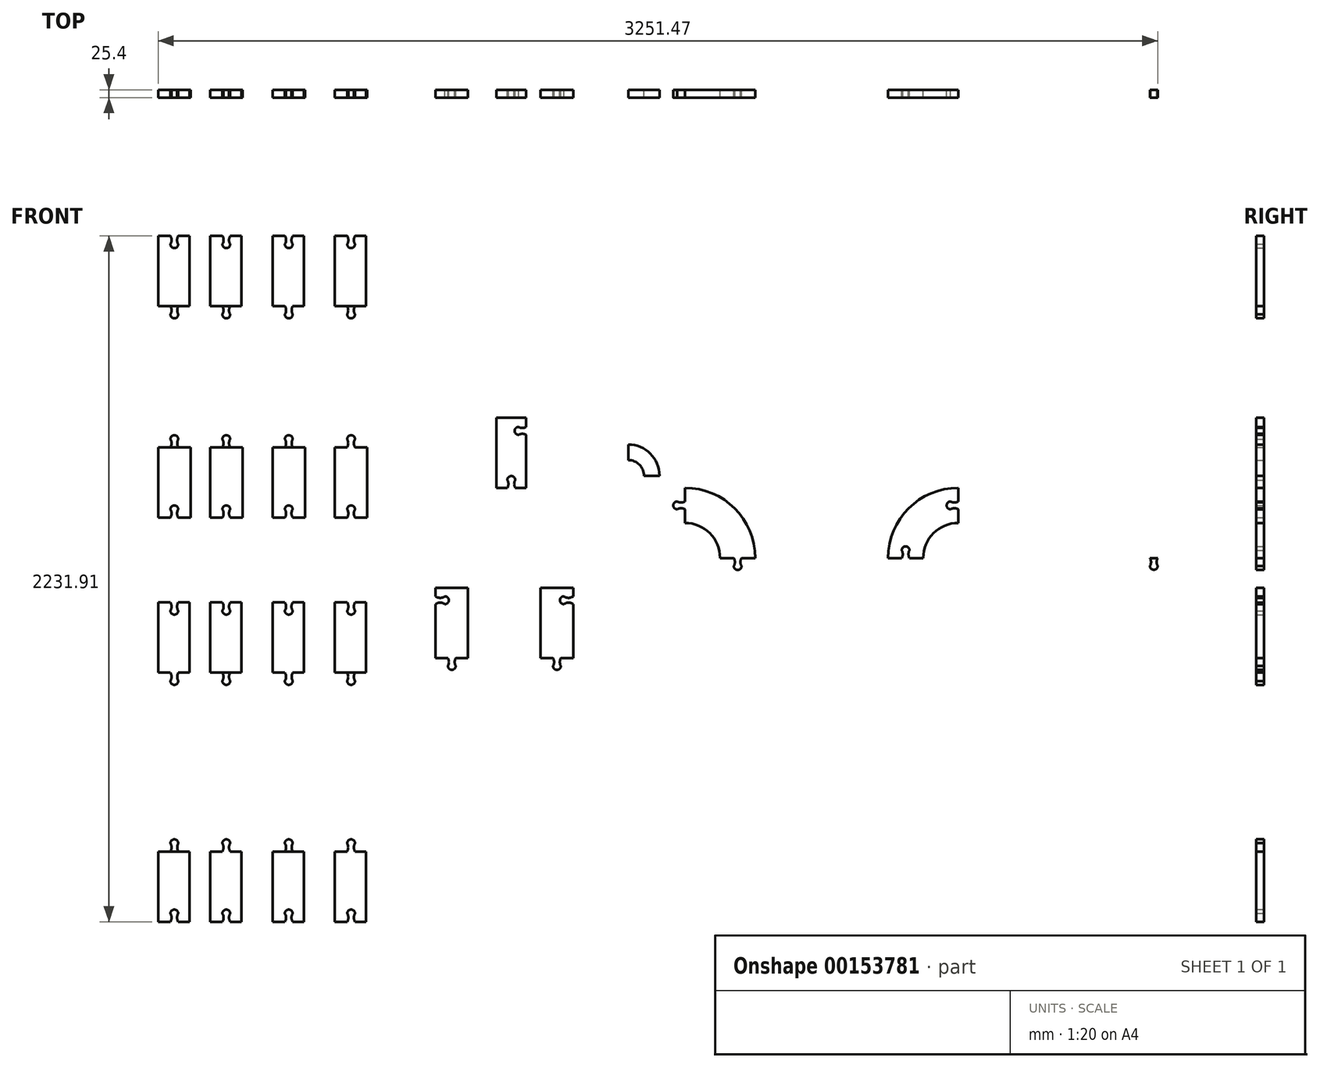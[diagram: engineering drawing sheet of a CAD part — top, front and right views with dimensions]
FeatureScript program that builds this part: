
annotation { "Feature Type Name" : "Feature", "Feature Type Description" : "" }
export const myFeature = defineFeature(function(context is Context, id is Id, definition is map)
    precondition{}
    {
        {
            var Q0;
            Q0=qCreatedBy(makeId("Front.planeOp"),FACE);
            var sketch = newSketch(context, id + "F0", { "sketchPlane" : qUnion([Q0])});
            skLineSegment(sketch, "E0", {"start": v(-147.56, 131.5) * mm, "end": v(-147.56, -97.1) * mm});
            skLineSegment(sketch, "E1", {"start": v(-147.56, 131.5) * mm, "end": v(-41.94, 131.5) * mm});
            skLineSegment(sketch, "E2", {"start": v(-41.94, 131.5) * mm, "end": v(-41.94, -97.1) * mm});
            skArc(sketch, "E3", {"start": v(-82.05, 158.39) * mm, "mid": v(-94.75, 171.09) * mm, "end": v(-107.45, 158.39) * mm});
            skArc(sketch, "E4", {"start": v(-107.45, 131.5) * mm, "mid": v(-103.6, 144.95) * mm, "end": v(-107.45, 158.39) * mm});
            skArc(sketch, "E5", {"start": v(-82.05, 158.39) * mm, "mid": v(-85.44, 144.95) * mm, "end": v(-82.05, 131.5) * mm});
            skPoint(sketch, "E6.start.orphan", {"position": v(-94.75, 131.5) * mm});
            skArc(sketch, "E7", {"start": v(-82.05, -70.22) * mm, "mid": v(-94.75, -57.52) * mm, "end": v(-107.45, -70.22) * mm});
            skArc(sketch, "E8", {"start": v(-107.45, -97.1) * mm, "mid": v(-103.6, -83.66) * mm, "end": v(-107.45, -70.22) * mm});
            skArc(sketch, "E9", {"start": v(-82.05, -70.22) * mm, "mid": v(-85.9, -83.66) * mm, "end": v(-82.05, -97.1) * mm});
            skPoint(sketch, "E10.start.orphan", {"position": v(-94.75, -97.1) * mm});
            skLineSegment(sketch, "E11", {"start": v(-147.56, -97.1) * mm, "end": v(-107.45, -97.1) * mm});
            skLineSegment(sketch, "E12", {"start": v(-82.05, -97.1) * mm, "end": v(-41.94, -97.1) * mm});
            skLineSegment(sketch, "E13", {"start": v(-10.22, 162) * mm, "end": v(-10.22, -91.05) * mm});
            skLineSegment(sketch, "E14.MirrorCS", {"start": v(61.6, -97.1) * mm, "end": v(21.5, -97.1) * mm});
            skArc(sketch, "E15.MirrorCS", {"start": v(61.6, 158.39) * mm, "mid": v(74.3, 171.09) * mm, "end": v(87, 158.39) * mm});
            skLineSegment(sketch, "E16.MirrorCS", {"start": v(127.12, -97.1) * mm, "end": v(87, -97.1) * mm});
            skArc(sketch, "E17.MirrorCS", {"start": v(61.6, -70.22) * mm, "mid": v(74.3, -57.52) * mm, "end": v(87, -70.22) * mm});
            skArc(sketch, "E18.MirrorCS", {"start": v(61.6, -70.22) * mm, "mid": v(65.45, -83.66) * mm, "end": v(61.6, -97.1) * mm});
            skArc(sketch, "E19.MirrorCS", {"start": v(87, -97.1) * mm, "mid": v(83.16, -83.66) * mm, "end": v(87, -70.22) * mm});
            skArc(sketch, "E20.MirrorCS", {"start": v(87, 131.5) * mm, "mid": v(83.16, 144.95) * mm, "end": v(87, 158.39) * mm});
            skArc(sketch, "E21.MirrorCS", {"start": v(61.6, 158.39) * mm, "mid": v(65, 144.95) * mm, "end": v(61.6, 131.5) * mm});
            skLineSegment(sketch, "E22.MirrorCS", {"start": v(127.12, 131.5) * mm, "end": v(21.5, 131.5) * mm});
            skLineSegment(sketch, "E23.MirrorCS", {"start": v(127.12, 131.5) * mm, "end": v(127.12, -97.1) * mm});
            skPoint(sketch, "E24.MirrorP", {"position": v(74.3, 131.5) * mm});
            skPoint(sketch, "E25.MirrorP", {"position": v(74.3, -97.1) * mm});
            skLineSegment(sketch, "E26.MirrorCS", {"start": v(21.5, 131.5) * mm, "end": v(21.5, -97.1) * mm});
            skLineSegment(sketch, "E27", {"start": v(175.89, 185.22) * mm, "end": v(175.89, -100.31) * mm});
            skArc(sketch, "E28.MirrorCS", {"start": v(290.17, -70.22) * mm, "mid": v(286.32, -83.66) * mm, "end": v(290.17, -97.1) * mm});
            skArc(sketch, "E29.MirrorCS", {"start": v(264.77, -97.1) * mm, "mid": v(268.61, -83.66) * mm, "end": v(264.77, -70.22) * mm});
            skArc(sketch, "E30.MirrorCS", {"start": v(290.17, 158.39) * mm, "mid": v(277.47, 171.09) * mm, "end": v(264.77, 158.39) * mm});
            skArc(sketch, "E31.MirrorCS", {"start": v(290.17, -70.22) * mm, "mid": v(277.47, -57.52) * mm, "end": v(264.77, -70.22) * mm});
            skLineSegment(sketch, "E32.MirrorCS", {"start": v(290.17, -97.1) * mm, "end": v(330.28, -97.1) * mm});
            skArc(sketch, "E33.MirrorCS", {"start": v(290.17, 158.39) * mm, "mid": v(286.78, 144.95) * mm, "end": v(290.17, 131.5) * mm});
            skLineSegment(sketch, "E34.MirrorCS", {"start": v(224.65, -97.1) * mm, "end": v(264.77, -97.1) * mm});
            skArc(sketch, "E35.MirrorCS", {"start": v(264.77, 131.5) * mm, "mid": v(268.61, 144.95) * mm, "end": v(264.77, 158.39) * mm});
            skLineSegment(sketch, "E36.MirrorCS", {"start": v(224.65, 131.5) * mm, "end": v(330.28, 131.5) * mm});
            skPoint(sketch, "E37.MirrorP", {"position": v(277.47, 131.5) * mm});
            skLineSegment(sketch, "E38.MirrorCS", {"start": v(224.65, 131.5) * mm, "end": v(224.65, -97.1) * mm});
            skPoint(sketch, "E39.MirrorP", {"position": v(277.47, -97.1) * mm});
            skLineSegment(sketch, "E40.MirrorCS", {"start": v(330.28, 131.5) * mm, "end": v(330.28, -97.1) * mm});
            skLineSegment(sketch, "E41", {"start": v(378.82, 155.95) * mm, "end": v(378.82, -86.6) * mm});
            skArc(sketch, "E42.MirrorCS", {"start": v(467.47, 158.39) * mm, "mid": v(480.17, 171.09) * mm, "end": v(492.87, 158.39) * mm});
            skArc(sketch, "E43.MirrorCS", {"start": v(467.47, -70.22) * mm, "mid": v(471.31, -83.66) * mm, "end": v(467.47, -97.1) * mm});
            skLineSegment(sketch, "E44.MirrorCS", {"start": v(467.47, -97.1) * mm, "end": v(427.35, -97.1) * mm});
            skLineSegment(sketch, "E45.MirrorCS", {"start": v(532.98, -97.1) * mm, "end": v(492.87, -97.1) * mm});
            skLineSegment(sketch, "E46.MirrorCS", {"start": v(532.98, 131.5) * mm, "end": v(532.98, -97.1) * mm});
            skPoint(sketch, "E47.MirrorP", {"position": v(480.17, -97.1) * mm});
            skArc(sketch, "E48.MirrorCS", {"start": v(467.47, -70.22) * mm, "mid": v(480.17, -57.52) * mm, "end": v(492.87, -70.22) * mm});
            skLineSegment(sketch, "E49.MirrorCS", {"start": v(532.98, 131.5) * mm, "end": v(427.35, 131.5) * mm});
            skArc(sketch, "E50.MirrorCS", {"start": v(492.87, -97.1) * mm, "mid": v(489.02, -83.66) * mm, "end": v(492.87, -70.22) * mm});
            skArc(sketch, "E51.MirrorCS", {"start": v(492.87, 131.5) * mm, "mid": v(489.02, 144.95) * mm, "end": v(492.87, 158.39) * mm});
            skArc(sketch, "E52.MirrorCS", {"start": v(467.47, 158.39) * mm, "mid": v(470.85, 144.95) * mm, "end": v(467.47, 131.5) * mm});
            skLineSegment(sketch, "E53.MirrorCS", {"start": v(427.35, 131.5) * mm, "end": v(427.35, -97.1) * mm});
            skPoint(sketch, "E54.MirrorP", {"position": v(480.17, 131.5) * mm});
            skArc(sketch, "E55.MirrorCS", {"start": v(-107.45, -373.24) * mm, "mid": v(-103.6, -386.68) * mm, "end": v(-107.45, -400.12) * mm});
            skArc(sketch, "E56.MirrorCS", {"start": v(-82.05, -400.12) * mm, "mid": v(-85.9, -386.68) * mm, "end": v(-82.05, -373.24) * mm});
            skArc(sketch, "E57.MirrorCS", {"start": v(264.77, -373.24) * mm, "mid": v(268.61, -386.68) * mm, "end": v(264.77, -400.12) * mm});
            skLineSegment(sketch, "E58.MirrorCS", {"start": v(61.6, -373.24) * mm, "end": v(21.5, -373.24) * mm});
            skArc(sketch, "E59.MirrorCS", {"start": v(492.87, -373.24) * mm, "mid": v(489.02, -386.68) * mm, "end": v(492.87, -400.12) * mm});
            skArc(sketch, "E60.MirrorCS", {"start": v(467.47, -628.73) * mm, "mid": v(470.85, -615.29) * mm, "end": v(467.47, -601.84) * mm});
            skArc(sketch, "E61.MirrorCS", {"start": v(61.6, -400.12) * mm, "mid": v(65.45, -386.68) * mm, "end": v(61.6, -373.24) * mm});
            skArc(sketch, "E62.MirrorCS", {"start": v(492.87, -601.84) * mm, "mid": v(489.02, -615.29) * mm, "end": v(492.87, -628.73) * mm});
            skLineSegment(sketch, "E63.MirrorCS", {"start": v(290.17, -373.24) * mm, "end": v(326.25, -373.24) * mm});
            skArc(sketch, "E64.MirrorCS", {"start": v(290.17, -400.12) * mm, "mid": v(286.32, -386.68) * mm, "end": v(290.17, -373.24) * mm});
            skArc(sketch, "E65.MirrorCS", {"start": v(467.47, -400.12) * mm, "mid": v(471.31, -386.68) * mm, "end": v(467.47, -373.24) * mm});
            skArc(sketch, "E66.MirrorCS", {"start": v(87, -373.24) * mm, "mid": v(83.16, -386.68) * mm, "end": v(87, -400.12) * mm});
            skArc(sketch, "E67.MirrorCS", {"start": v(467.47, -400.12) * mm, "mid": v(480.17, -412.82) * mm, "end": v(492.87, -400.12) * mm});
            skArc(sketch, "E68.MirrorCS", {"start": v(87, -601.84) * mm, "mid": v(83.16, -615.29) * mm, "end": v(87, -628.73) * mm});
            skLineSegment(sketch, "E69.MirrorCS", {"start": v(528.95, -601.84) * mm, "end": v(427.35, -601.84) * mm});
            skArc(sketch, "E70.MirrorCS", {"start": v(290.17, -628.73) * mm, "mid": v(277.47, -641.43) * mm, "end": v(264.77, -628.73) * mm});
            skArc(sketch, "E71.MirrorCS", {"start": v(61.6, -628.73) * mm, "mid": v(65, -615.29) * mm, "end": v(61.6, -601.84) * mm});
            skArc(sketch, "E72.MirrorCS", {"start": v(61.6, -628.73) * mm, "mid": v(74.3, -641.43) * mm, "end": v(87, -628.73) * mm});
            skLineSegment(sketch, "E73.MirrorCS", {"start": v(123.1, -373.24) * mm, "end": v(87, -373.24) * mm});
            skArc(sketch, "E74.MirrorCS", {"start": v(61.6, -400.12) * mm, "mid": v(74.3, -412.82) * mm, "end": v(87, -400.12) * mm});
            skLineSegment(sketch, "E75.MirrorCS", {"start": v(-147.56, -601.84) * mm, "end": v(-45.96, -601.84) * mm});
            skArc(sketch, "E76.MirrorCS", {"start": v(-82.05, -628.73) * mm, "mid": v(-94.75, -641.43) * mm, "end": v(-107.45, -628.73) * mm});
            skArc(sketch, "E77.MirrorCS", {"start": v(-107.45, -601.84) * mm, "mid": v(-103.6, -615.29) * mm, "end": v(-107.45, -628.73) * mm});
            skArc(sketch, "E78.MirrorCS", {"start": v(-82.05, -628.73) * mm, "mid": v(-85.44, -615.29) * mm, "end": v(-82.05, -601.84) * mm});
            skArc(sketch, "E79.MirrorCS", {"start": v(-82.05, -400.12) * mm, "mid": v(-94.75, -412.82) * mm, "end": v(-107.45, -400.12) * mm});
            skLineSegment(sketch, "E80.MirrorCS", {"start": v(-147.56, -373.24) * mm, "end": v(-107.45, -373.24) * mm});
            skLineSegment(sketch, "E81.MirrorCS", {"start": v(-82.05, -373.24) * mm, "end": v(-45.96, -373.24) * mm});
            skArc(sketch, "E82.MirrorCS", {"start": v(290.17, -400.12) * mm, "mid": v(277.47, -412.82) * mm, "end": v(264.77, -400.12) * mm});
            skLineSegment(sketch, "E83.MirrorCS", {"start": v(528.95, -373.24) * mm, "end": v(492.87, -373.24) * mm});
            skLineSegment(sketch, "E84.MirrorCS", {"start": v(123.1, -601.84) * mm, "end": v(21.5, -601.84) * mm});
            skArc(sketch, "E85.MirrorCS", {"start": v(467.47, -628.73) * mm, "mid": v(480.17, -641.43) * mm, "end": v(492.87, -628.73) * mm});
            skArc(sketch, "E86.MirrorCS", {"start": v(290.17, -628.73) * mm, "mid": v(286.78, -615.29) * mm, "end": v(290.17, -601.84) * mm});
            skLineSegment(sketch, "E87.MirrorCS", {"start": v(224.65, -601.84) * mm, "end": v(326.25, -601.84) * mm});
            skLineSegment(sketch, "E88.MirrorCS", {"start": v(224.65, -373.24) * mm, "end": v(264.77, -373.24) * mm});
            skLineSegment(sketch, "E89.MirrorCS", {"start": v(467.47, -373.24) * mm, "end": v(427.35, -373.24) * mm});
            skArc(sketch, "E90.MirrorCS", {"start": v(264.77, -601.84) * mm, "mid": v(268.61, -615.29) * mm, "end": v(264.77, -628.73) * mm});
            skLineSegment(sketch, "E91.MirrorCS", {"start": v(21.5, -601.84) * mm, "end": v(21.5, -373.24) * mm});
            skLineSegment(sketch, "E92.MirrorCS", {"start": v(326.25, -601.84) * mm, "end": v(326.25, -373.24) * mm});
            skPoint(sketch, "E93.MirrorP", {"position": v(-94.75, -601.84) * mm});
            skLineSegment(sketch, "E94.MirrorCS", {"start": v(378.82, -626.3) * mm, "end": v(378.82, -383.74) * mm});
            skPoint(sketch, "E95.MirrorP", {"position": v(480.17, -373.24) * mm});
            skLineSegment(sketch, "E96.MirrorCS", {"start": v(-147.56, -601.84) * mm, "end": v(-147.56, -373.24) * mm});
            skLineSegment(sketch, "E97.MirrorCS", {"start": v(-45.96, -601.84) * mm, "end": v(-45.96, -373.24) * mm});
            skLineSegment(sketch, "E98.MirrorCS", {"start": v(-10.22, -632.34) * mm, "end": v(-10.22, -379.29) * mm});
            skPoint(sketch, "E99.MirrorP", {"position": v(277.47, -373.24) * mm});
            skLineSegment(sketch, "E100.MirrorCS", {"start": v(175.89, -655.56) * mm, "end": v(175.89, -370.02) * mm});
            skPoint(sketch, "E101.MirrorP", {"position": v(-94.75, -373.24) * mm});
            skPoint(sketch, "E102.MirrorP", {"position": v(74.3, -601.84) * mm});
            skLineSegment(sketch, "E103.MirrorCS", {"start": v(528.95, -601.84) * mm, "end": v(528.95, -373.24) * mm});
            skLineSegment(sketch, "E104.MirrorCS", {"start": v(123.1, -601.84) * mm, "end": v(123.1, -373.24) * mm});
            skLineSegment(sketch, "E105.MirrorCS", {"start": v(427.35, -601.84) * mm, "end": v(427.35, -373.24) * mm});
            skLineSegment(sketch, "E106.MirrorCS", {"start": v(224.65, -601.84) * mm, "end": v(224.65, -373.24) * mm});
            skPoint(sketch, "E107.MirrorP", {"position": v(480.17, -601.84) * mm});
            skPoint(sketch, "E108.MirrorP", {"position": v(74.3, -373.24) * mm});
            skPoint(sketch, "E109.MirrorP", {"position": v(277.47, -601.84) * mm});
            skArc(sketch, "E110.MirrorCS", {"start": v(290.17, -1385.47) * mm, "mid": v(286.32, -1398.9) * mm, "end": v(290.17, -1412.34) * mm});
            skArc(sketch, "E111.MirrorCS", {"start": v(-82.05, -1385.47) * mm, "mid": v(-85.9, -1398.9) * mm, "end": v(-82.05, -1412.34) * mm});
            skArc(sketch, "E112.MirrorCS", {"start": v(-107.45, -1412.34) * mm, "mid": v(-103.6, -1398.9) * mm, "end": v(-107.45, -1385.47) * mm});
            skArc(sketch, "E113.MirrorCS", {"start": v(264.77, -1412.34) * mm, "mid": v(268.61, -1398.9) * mm, "end": v(264.77, -1385.47) * mm});
            skLineSegment(sketch, "E114.MirrorCS", {"start": v(-82.05, -1412.34) * mm, "end": v(-45.96, -1412.34) * mm});
            skArc(sketch, "E115.MirrorCS", {"start": v(61.6, -1156.86) * mm, "mid": v(74.3, -1144.16) * mm, "end": v(87, -1156.86) * mm});
            skArc(sketch, "E116.MirrorCS", {"start": v(-82.05, -1385.47) * mm, "mid": v(-94.75, -1372.77) * mm, "end": v(-107.45, -1385.47) * mm});
            skLineSegment(sketch, "E117.MirrorCS", {"start": v(290.17, -1412.34) * mm, "end": v(326.25, -1412.34) * mm});
            skArc(sketch, "E118.MirrorCS", {"start": v(61.6, -1156.86) * mm, "mid": v(65, -1170.3) * mm, "end": v(61.6, -1183.74) * mm});
            skArc(sketch, "E119.MirrorCS", {"start": v(-82.05, -1156.86) * mm, "mid": v(-85.44, -1170.3) * mm, "end": v(-82.05, -1183.74) * mm});
            skArc(sketch, "E120.MirrorCS", {"start": v(61.6, -1385.47) * mm, "mid": v(65.45, -1398.9) * mm, "end": v(61.6, -1412.34) * mm});
            skArc(sketch, "E121.MirrorCS", {"start": v(-107.45, -1183.74) * mm, "mid": v(-103.6, -1170.3) * mm, "end": v(-107.45, -1156.86) * mm});
            skArc(sketch, "E122.MirrorCS", {"start": v(492.87, -1412.34) * mm, "mid": v(489.02, -1398.9) * mm, "end": v(492.87, -1385.47) * mm});
            skArc(sketch, "E123.MirrorCS", {"start": v(87, -1183.74) * mm, "mid": v(83.16, -1170.3) * mm, "end": v(87, -1156.86) * mm});
            skArc(sketch, "E124.MirrorCS", {"start": v(290.17, -1385.47) * mm, "mid": v(277.47, -1372.77) * mm, "end": v(264.77, -1385.47) * mm});
            skArc(sketch, "E125.MirrorCS", {"start": v(87, -1412.34) * mm, "mid": v(83.16, -1398.9) * mm, "end": v(87, -1385.47) * mm});
            skArc(sketch, "E126.MirrorCS", {"start": v(-82.05, -1156.86) * mm, "mid": v(-94.75, -1144.16) * mm, "end": v(-107.45, -1156.86) * mm});
            skLineSegment(sketch, "E127.MirrorCS", {"start": v(528.95, -1412.34) * mm, "end": v(492.87, -1412.34) * mm});
            skArc(sketch, "E128.MirrorCS", {"start": v(467.47, -1385.47) * mm, "mid": v(480.17, -1372.77) * mm, "end": v(492.87, -1385.47) * mm});
            skArc(sketch, "E129.MirrorCS", {"start": v(61.6, -1385.47) * mm, "mid": v(74.3, -1372.77) * mm, "end": v(87, -1385.47) * mm});
            skArc(sketch, "E130.MirrorCS", {"start": v(467.47, -1385.47) * mm, "mid": v(471.31, -1398.9) * mm, "end": v(467.47, -1412.34) * mm});
            skLineSegment(sketch, "E131.MirrorCS", {"start": v(467.47, -1412.34) * mm, "end": v(427.35, -1412.34) * mm});
            skLineSegment(sketch, "E132.MirrorCS", {"start": v(-147.56, -1412.34) * mm, "end": v(-107.45, -1412.34) * mm});
            skLineSegment(sketch, "E133.MirrorCS", {"start": v(224.65, -1412.34) * mm, "end": v(264.77, -1412.34) * mm});
            skLineSegment(sketch, "E134.MirrorCS", {"start": v(224.65, -1183.74) * mm, "end": v(326.25, -1183.74) * mm});
            skArc(sketch, "E135.MirrorCS", {"start": v(492.87, -1183.74) * mm, "mid": v(489.02, -1170.3) * mm, "end": v(492.87, -1156.86) * mm});
            skArc(sketch, "E136.MirrorCS", {"start": v(290.17, -1156.86) * mm, "mid": v(277.47, -1144.16) * mm, "end": v(264.77, -1156.86) * mm});
            skArc(sketch, "E137.MirrorCS", {"start": v(290.17, -1156.86) * mm, "mid": v(286.78, -1170.3) * mm, "end": v(290.17, -1183.74) * mm});
            skLineSegment(sketch, "E138.MirrorCS", {"start": v(-147.56, -1183.74) * mm, "end": v(-45.96, -1183.74) * mm});
            skArc(sketch, "E139.MirrorCS", {"start": v(467.47, -1156.86) * mm, "mid": v(470.85, -1170.3) * mm, "end": v(467.47, -1183.74) * mm});
            skLineSegment(sketch, "E140.MirrorCS", {"start": v(123.1, -1183.74) * mm, "end": v(21.5, -1183.74) * mm});
            skLineSegment(sketch, "E141.MirrorCS", {"start": v(528.95, -1183.74) * mm, "end": v(427.35, -1183.74) * mm});
            skArc(sketch, "E142.MirrorCS", {"start": v(467.47, -1156.86) * mm, "mid": v(480.17, -1144.16) * mm, "end": v(492.87, -1156.86) * mm});
            skLineSegment(sketch, "E143.MirrorCS", {"start": v(61.6, -1412.34) * mm, "end": v(21.5, -1412.34) * mm});
            skLineSegment(sketch, "E144.MirrorCS", {"start": v(123.1, -1412.34) * mm, "end": v(87, -1412.34) * mm});
            skArc(sketch, "E145.MirrorCS", {"start": v(264.77, -1183.74) * mm, "mid": v(268.61, -1170.3) * mm, "end": v(264.77, -1156.86) * mm});
            skLineSegment(sketch, "E146.MirrorCS", {"start": v(-10.22, -1153.24) * mm, "end": v(-10.22, -1406.3) * mm});
            skPoint(sketch, "E147.MirrorP", {"position": v(480.17, -1412.34) * mm});
            skLineSegment(sketch, "E148.MirrorCS", {"start": v(-45.96, -1183.74) * mm, "end": v(-45.96, -1412.34) * mm});
            skPoint(sketch, "E149.MirrorP", {"position": v(-94.75, -1183.74) * mm});
            skLineSegment(sketch, "E150.MirrorCS", {"start": v(-147.56, -1183.74) * mm, "end": v(-147.56, -1412.34) * mm});
            skLineSegment(sketch, "E151.MirrorCS", {"start": v(378.82, -1159.3) * mm, "end": v(378.82, -1401.84) * mm});
            skPoint(sketch, "E152.MirrorP", {"position": v(277.47, -1183.74) * mm});
            skLineSegment(sketch, "E153.MirrorCS", {"start": v(427.35, -1183.74) * mm, "end": v(427.35, -1412.34) * mm});
            skPoint(sketch, "E154.MirrorP", {"position": v(74.3, -1183.74) * mm});
            skLineSegment(sketch, "E155.MirrorCS", {"start": v(224.65, -1183.74) * mm, "end": v(224.65, -1412.34) * mm});
            skLineSegment(sketch, "E156.MirrorCS", {"start": v(21.5, -1183.74) * mm, "end": v(21.5, -1412.34) * mm});
            skLineSegment(sketch, "E157.MirrorCS", {"start": v(528.95, -1183.74) * mm, "end": v(528.95, -1412.34) * mm});
            skPoint(sketch, "E158.MirrorP", {"position": v(480.17, -1183.74) * mm});
            skLineSegment(sketch, "E159.MirrorCS", {"start": v(326.25, -1183.74) * mm, "end": v(326.25, -1412.34) * mm});
            skLineSegment(sketch, "E160.MirrorCS", {"start": v(123.1, -1183.74) * mm, "end": v(123.1, -1412.34) * mm});
            skPoint(sketch, "E161.MirrorP", {"position": v(277.47, -1412.34) * mm});
            skPoint(sketch, "E162.MirrorP", {"position": v(74.3, -1412.34) * mm});
            skLineSegment(sketch, "E163.MirrorCS", {"start": v(175.89, -1130.03) * mm, "end": v(175.89, -1415.56) * mm});
            skPoint(sketch, "E164.MirrorP", {"position": v(-94.75, -1412.34) * mm});
            skArc(sketch, "E165.MirrorCS", {"start": v(61.6, 564.08) * mm, "mid": v(65, 577.53) * mm, "end": v(61.6, 590.97) * mm});
            skLineSegment(sketch, "E166.MirrorCS", {"start": v(123.1, 590.97) * mm, "end": v(21.5, 590.97) * mm});
            skArc(sketch, "E167.MirrorCS", {"start": v(467.47, 564.08) * mm, "mid": v(480.17, 551.38) * mm, "end": v(492.87, 564.08) * mm});
            skArc(sketch, "E168.MirrorCS", {"start": v(87, 590.97) * mm, "mid": v(83.16, 577.53) * mm, "end": v(87, 564.08) * mm});
            skArc(sketch, "E169.MirrorCS", {"start": v(290.17, 564.08) * mm, "mid": v(286.78, 577.53) * mm, "end": v(290.17, 590.97) * mm});
            skArc(sketch, "E170.MirrorCS", {"start": v(467.47, 564.08) * mm, "mid": v(470.85, 577.53) * mm, "end": v(467.47, 590.97) * mm});
            skArc(sketch, "E171.MirrorCS", {"start": v(87, 819.57) * mm, "mid": v(83.16, 806.13) * mm, "end": v(87, 792.7) * mm});
            skArc(sketch, "E172.MirrorCS", {"start": v(61.6, 792.7) * mm, "mid": v(65.45, 806.13) * mm, "end": v(61.6, 819.57) * mm});
            skLineSegment(sketch, "E173.MirrorCS", {"start": v(61.6, 819.57) * mm, "end": v(21.5, 819.57) * mm});
            skLineSegment(sketch, "E174.MirrorCS", {"start": v(-82.05, 819.57) * mm, "end": v(-45.96, 819.57) * mm});
            skLineSegment(sketch, "E175.MirrorCS", {"start": v(-147.56, 819.57) * mm, "end": v(-107.45, 819.57) * mm});
            skArc(sketch, "E176.MirrorCS", {"start": v(-82.05, 792.7) * mm, "mid": v(-85.9, 806.13) * mm, "end": v(-82.05, 819.57) * mm});
            skArc(sketch, "E177.MirrorCS", {"start": v(-107.45, 819.57) * mm, "mid": v(-103.6, 806.13) * mm, "end": v(-107.45, 792.7) * mm});
            skArc(sketch, "E178.MirrorCS", {"start": v(-82.05, 792.7) * mm, "mid": v(-94.75, 780) * mm, "end": v(-107.45, 792.7) * mm});
            skArc(sketch, "E179.MirrorCS", {"start": v(-82.05, 564.08) * mm, "mid": v(-85.44, 577.53) * mm, "end": v(-82.05, 590.97) * mm});
            skArc(sketch, "E180.MirrorCS", {"start": v(-107.45, 590.97) * mm, "mid": v(-103.6, 577.53) * mm, "end": v(-107.45, 564.08) * mm});
            skArc(sketch, "E181.MirrorCS", {"start": v(-82.05, 564.08) * mm, "mid": v(-94.75, 551.38) * mm, "end": v(-107.45, 564.08) * mm});
            skArc(sketch, "E182.MirrorCS", {"start": v(61.6, 564.08) * mm, "mid": v(74.3, 551.38) * mm, "end": v(87, 564.08) * mm});
            skArc(sketch, "E183.MirrorCS", {"start": v(264.77, 590.97) * mm, "mid": v(268.61, 577.53) * mm, "end": v(264.77, 564.08) * mm});
            skArc(sketch, "E184.MirrorCS", {"start": v(492.87, 590.97) * mm, "mid": v(489.02, 577.53) * mm, "end": v(492.87, 564.08) * mm});
            skArc(sketch, "E185.MirrorCS", {"start": v(290.17, 564.08) * mm, "mid": v(277.47, 551.38) * mm, "end": v(264.77, 564.08) * mm});
            skArc(sketch, "E186.MirrorCS", {"start": v(467.47, 792.7) * mm, "mid": v(471.31, 806.13) * mm, "end": v(467.47, 819.57) * mm});
            skLineSegment(sketch, "E187.MirrorCS", {"start": v(467.47, 819.57) * mm, "end": v(427.35, 819.57) * mm});
            skLineSegment(sketch, "E188.MirrorCS", {"start": v(528.95, 819.57) * mm, "end": v(492.87, 819.57) * mm});
            skArc(sketch, "E189.MirrorCS", {"start": v(290.17, 792.7) * mm, "mid": v(286.32, 806.13) * mm, "end": v(290.17, 819.57) * mm});
            skArc(sketch, "E190.MirrorCS", {"start": v(290.17, 792.7) * mm, "mid": v(277.47, 780) * mm, "end": v(264.77, 792.7) * mm});
            skArc(sketch, "E191.MirrorCS", {"start": v(492.87, 819.57) * mm, "mid": v(489.02, 806.13) * mm, "end": v(492.87, 792.7) * mm});
            skLineSegment(sketch, "E192.MirrorCS", {"start": v(224.65, 590.97) * mm, "end": v(326.25, 590.97) * mm});
            skLineSegment(sketch, "E193.MirrorCS", {"start": v(-147.56, 590.97) * mm, "end": v(-45.96, 590.97) * mm});
            skLineSegment(sketch, "E194.MirrorCS", {"start": v(123.1, 819.57) * mm, "end": v(87, 819.57) * mm});
            skLineSegment(sketch, "E195.MirrorCS", {"start": v(224.65, 819.57) * mm, "end": v(264.77, 819.57) * mm});
            skLineSegment(sketch, "E196.MirrorCS", {"start": v(290.17, 819.57) * mm, "end": v(326.25, 819.57) * mm});
            skArc(sketch, "E197.MirrorCS", {"start": v(264.77, 819.57) * mm, "mid": v(268.61, 806.13) * mm, "end": v(264.77, 792.7) * mm});
            skLineSegment(sketch, "E198.MirrorCS", {"start": v(528.95, 590.97) * mm, "end": v(427.35, 590.97) * mm});
            skArc(sketch, "E199.MirrorCS", {"start": v(61.6, 792.7) * mm, "mid": v(74.3, 780) * mm, "end": v(87, 792.7) * mm});
            skArc(sketch, "E200.MirrorCS", {"start": v(467.47, 792.7) * mm, "mid": v(480.17, 780) * mm, "end": v(492.87, 792.7) * mm});
            skPoint(sketch, "E201.MirrorP", {"position": v(-94.75, 590.97) * mm});
            skLineSegment(sketch, "E202.MirrorCS", {"start": v(378.82, 566.52) * mm, "end": v(378.82, 809.07) * mm});
            skLineSegment(sketch, "E203.MirrorCS", {"start": v(123.1, 590.97) * mm, "end": v(123.1, 819.57) * mm});
            skPoint(sketch, "E204.MirrorP", {"position": v(277.47, 590.97) * mm});
            skLineSegment(sketch, "E205.MirrorCS", {"start": v(21.5, 590.97) * mm, "end": v(21.5, 819.57) * mm});
            skPoint(sketch, "E206.MirrorP", {"position": v(-94.75, 819.57) * mm});
            skPoint(sketch, "E207.MirrorP", {"position": v(277.47, 819.57) * mm});
            skLineSegment(sketch, "E208.MirrorCS", {"start": v(175.89, 537.25) * mm, "end": v(175.89, 822.79) * mm});
            skLineSegment(sketch, "E209.MirrorCS", {"start": v(528.95, 590.97) * mm, "end": v(528.95, 819.57) * mm});
            skLineSegment(sketch, "E210.MirrorCS", {"start": v(224.65, 590.97) * mm, "end": v(224.65, 819.57) * mm});
            skLineSegment(sketch, "E211.MirrorCS", {"start": v(-10.22, 560.47) * mm, "end": v(-10.22, 813.53) * mm});
            skLineSegment(sketch, "E212.MirrorCS", {"start": v(326.25, 590.97) * mm, "end": v(326.25, 819.57) * mm});
            skLineSegment(sketch, "E213.MirrorCS", {"start": v(-45.96, 590.97) * mm, "end": v(-45.96, 819.57) * mm});
            skLineSegment(sketch, "E214.MirrorCS", {"start": v(-147.56, 590.97) * mm, "end": v(-147.56, 819.57) * mm});
            skLineSegment(sketch, "E215.MirrorCS", {"start": v(427.35, 590.97) * mm, "end": v(427.35, 819.57) * mm});
            skPoint(sketch, "E216.MirrorP", {"position": v(74.3, 819.57) * mm});
            skPoint(sketch, "E217.MirrorP", {"position": v(480.17, 590.97) * mm});
            skPoint(sketch, "E218.MirrorP", {"position": v(74.3, 590.97) * mm});
            skPoint(sketch, "E219.MirrorP", {"position": v(480.17, 819.57) * mm});
            skLineSegment(sketch, "E220", {"start": v(1049.52, 228.6) * mm, "end": v(952.96, 228.6) * mm});
            skLineSegment(sketch, "E221", {"start": v(952.96, 228.6) * mm, "end": v(952.96, 127) * mm});
            skLineSegment(sketch, "E222", {"start": v(952.96, 101.6) * mm, "end": v(952.96, 0) * mm});
            skLineSegment(sketch, "E223", {"start": v(1049.52, 0) * mm, "end": v(1049.52, 101.6) * mm});
            skLineSegment(sketch, "E224", {"start": v(902.32, -54.31) * mm, "end": v(1094.12, -54.31) * mm});
            skArc(sketch, "E225", {"start": v(1049.52, 172.48) * mm, "mid": v(1037.2, 175.67) * mm, "end": v(1024.88, 172.48) * mm});
            skArc(sketch, "E226", {"start": v(1024.88, 197.88) * mm, "mid": v(1037.2, 194.7) * mm, "end": v(1049.52, 197.88) * mm});
            skArc(sketch, "E227", {"start": v(1024.88, 197.88) * mm, "mid": v(1011.95, 185.18) * mm, "end": v(1024.88, 172.48) * mm});
            skLineSegment(sketch, "E228", {"start": v(1049.52, 228.6) * mm, "end": v(1049.52, 197.88) * mm});
            skLineSegment(sketch, "E229", {"start": v(1049.52, 172.48) * mm, "end": v(1049.52, 127) * mm});
            skLineSegment(sketch, "E230", {"start": v(1049.52, 127) * mm, "end": v(1049.52, 101.6) * mm});
            skLineSegment(sketch, "E231", {"start": v(952.96, 127) * mm, "end": v(952.96, 101.6) * mm});
            skArc(sketch, "E232", {"start": v(1013.94, 25.4) * mm, "mid": v(1010.53, 12.7) * mm, "end": v(1013.94, 0) * mm});
            skArc(sketch, "E233", {"start": v(988.54, 0) * mm, "mid": v(991.94, 12.7) * mm, "end": v(988.54, 25.4) * mm});
            skArc(sketch, "E234", {"start": v(1013.94, 25.4) * mm, "mid": v(1001.24, 38.22) * mm, "end": v(988.54, 25.4) * mm});
            skLineSegment(sketch, "E235", {"start": v(952.96, 0) * mm, "end": v(988.54, 0) * mm});
            skLineSegment(sketch, "E236", {"start": v(1013.94, 0) * mm, "end": v(1049.52, 0) * mm});
            skLineSegment(sketch, "E237", {"start": v(754.98, -554.52) * mm, "end": v(860.59, -554.52) * mm});
            skLineSegment(sketch, "E238", {"start": v(860.59, -325.92) * mm, "end": v(754.98, -325.92) * mm});
            skArc(sketch, "E239", {"start": v(795.08, -579.92) * mm, "mid": v(798.49, -567.22) * mm, "end": v(795.08, -554.52) * mm});
            skArc(sketch, "E240", {"start": v(820.48, -554.52) * mm, "mid": v(817.08, -567.22) * mm, "end": v(820.48, -579.92) * mm});
            skArc(sketch, "E241", {"start": v(795.08, -579.92) * mm, "mid": v(807.78, -592.63) * mm, "end": v(820.48, -579.92) * mm});
            skLineSegment(sketch, "E242", {"start": v(860.59, -554.52) * mm, "end": v(860.59, -378.72) * mm});
            skLineSegment(sketch, "E243", {"start": v(860.59, -353.32) * mm, "end": v(860.59, -325.92) * mm});
            skArc(sketch, "E244.MirrorCS", {"start": v(785.12, -353.32) * mm, "mid": v(798, -366.02) * mm, "end": v(785.12, -378.72) * mm});
            skArc(sketch, "E245.MirrorCS", {"start": v(754.98, -378.72) * mm, "mid": v(770.05, -373.77) * mm, "end": v(785.12, -378.72) * mm});
            skArc(sketch, "E246.MirrorCS", {"start": v(785.12, -353.32) * mm, "mid": v(770.05, -358.28) * mm, "end": v(754.98, -353.32) * mm});
            skLineSegment(sketch, "E247.MirrorCS", {"start": v(754.98, -353.32) * mm, "end": v(754.98, -325.92) * mm});
            skLineSegment(sketch, "E248.MirrorCS", {"start": v(754.98, -554.52) * mm, "end": v(754.98, -378.72) * mm});
            skLineSegment(sketch, "E249", {"start": v(860.59, -353.32) * mm, "end": v(860.59, -378.72) * mm});
            skLineSegment(sketch, "E250", {"start": v(978.73, -288.84) * mm, "end": v(978.73, -655.33) * mm});
            skArc(sketch, "E251.MirrorCS", {"start": v(1172.34, -353.32) * mm, "mid": v(1159.47, -366.02) * mm, "end": v(1172.34, -378.72) * mm});
            skArc(sketch, "E252.MirrorCS", {"start": v(1172.34, -353.32) * mm, "mid": v(1187.41, -358.28) * mm, "end": v(1202.48, -353.32) * mm});
            skArc(sketch, "E253.MirrorCS", {"start": v(1202.48, -378.72) * mm, "mid": v(1187.41, -373.77) * mm, "end": v(1172.34, -378.72) * mm});
            skLineSegment(sketch, "E254.MirrorCS", {"start": v(1096.87, -353.32) * mm, "end": v(1096.87, -325.92) * mm});
            skArc(sketch, "E255.MirrorCS", {"start": v(1136.97, -554.52) * mm, "mid": v(1140.38, -567.22) * mm, "end": v(1136.97, -579.92) * mm});
            skArc(sketch, "E256.MirrorCS", {"start": v(1162.37, -579.92) * mm, "mid": v(1149.67, -592.63) * mm, "end": v(1136.97, -579.92) * mm});
            skArc(sketch, "E257.MirrorCS", {"start": v(1162.37, -579.92) * mm, "mid": v(1158.97, -567.22) * mm, "end": v(1162.37, -554.52) * mm});
            skLineSegment(sketch, "E258.MirrorCS", {"start": v(1202.48, -353.32) * mm, "end": v(1202.48, -325.92) * mm});
            skLineSegment(sketch, "E259.MirrorCS", {"start": v(1202.48, -554.52) * mm, "end": v(1096.87, -554.52) * mm});
            skLineSegment(sketch, "E260.MirrorCS", {"start": v(1096.87, -554.52) * mm, "end": v(1096.87, -378.72) * mm});
            skLineSegment(sketch, "E261.MirrorCS", {"start": v(1096.87, -325.92) * mm, "end": v(1202.48, -325.92) * mm});
            skLineSegment(sketch, "E262.MirrorCS", {"start": v(1202.48, -554.52) * mm, "end": v(1202.48, -378.72) * mm});
            skLineSegment(sketch, "E263", {"start": v(1149.67, -325.92) * mm, "end": v(1149.67, -398.8) * mm});
            skArc(sketch, "E264.MirrorCS", {"start": v(1127, -353.32) * mm, "mid": v(1111.94, -358.28) * mm, "end": v(1096.87, -353.32) * mm});
            skArc(sketch, "E265.MirrorCS", {"start": v(1127, -353.32) * mm, "mid": v(1139.88, -366.02) * mm, "end": v(1127, -378.72) * mm});
            skArc(sketch, "E266.MirrorCS", {"start": v(1096.87, -378.72) * mm, "mid": v(1111.94, -373.77) * mm, "end": v(1127, -378.72) * mm});
            skLineSegment(sketch, "E267", {"start": v(1096.87, -353.32) * mm, "end": v(1096.87, -378.72) * mm});
            skArc(sketch, "E268", {"start": v(1432.5, 39.22) * mm, "mid": v(1417.63, 75.14) * mm, "end": v(1381.7, 90.02) * mm});
            skArc(sketch, "E269", {"start": v(1483.3, 39.22) * mm, "mid": v(1453.55, 111.06) * mm, "end": v(1381.7, 140.82) * mm});
            skLineSegment(sketch, "E270", {"start": v(1381.7, 140.82) * mm, "end": v(1381.7, 90.02) * mm});
            skLineSegment(sketch, "E271", {"start": v(1483.3, 39.22) * mm, "end": v(1432.5, 39.22) * mm});
            skSolve(sketch);
        }
        {
            var Q0;
            Q0=makeQuery(id+"F0.imprint","IMPRINT",FACE,{"disambiguationData":[TD([[makeQuery(id+"F0.imprint","IMPRINT",EDGE,{"derivedFrom":sQuery(id+"F0.wireOp",EDGE,"E174.MirrorCS")}),-1.0]])]});
            var Q1;
            Q1=makeQuery(id+"F0.imprint","IMPRINT",FACE,{"disambiguationData":[TD([[makeQuery(id+"F0.imprint","IMPRINT",EDGE,{"derivedFrom":sQuery(id+"F0.wireOp",EDGE,"E171.MirrorCS")}),1.0]])]});
            var Q2;
            Q2=makeQuery(id+"F0.imprint","IMPRINT",FACE,{"disambiguationData":[TD([[makeQuery(id+"F0.imprint","IMPRINT",EDGE,{"derivedFrom":sQuery(id+"F0.wireOp",EDGE,"E189.MirrorCS")}),-1.0]])]});
            var Q3;
            Q3=makeQuery(id+"F0.imprint","IMPRINT",FACE,{"disambiguationData":[TD([[makeQuery(id+"F0.imprint","IMPRINT",EDGE,{"derivedFrom":sQuery(id+"F0.wireOp",EDGE,"E186.MirrorCS")}),1.0]])]});
            var Q4;
            Q4=makeQuery(id+"F0.imprint","IMPRINT",FACE,{"disambiguationData":[TD([[makeQuery(id+"F0.imprint","IMPRINT",EDGE,{"derivedFrom":sQuery(id+"F0.wireOp",EDGE,"E43.MirrorCS")}),-1.0]])]});
            var Q5;
            Q5=makeQuery(id+"F0.imprint","IMPRINT",FACE,{"disambiguationData":[TD([[makeQuery(id+"F0.imprint","IMPRINT",EDGE,{"derivedFrom":sQuery(id+"F0.wireOp",EDGE,"E28.MirrorCS")}),1.0]])]});
            var Q6;
            Q6=makeQuery(id+"F0.imprint","IMPRINT",FACE,{"disambiguationData":[TD([[makeQuery(id+"F0.imprint","IMPRINT",EDGE,{"derivedFrom":sQuery(id+"F0.wireOp",EDGE,"E14.MirrorCS")}),-1.0]])]});
            var Q7;
            {var subQ4=sQuery(id+"F0.wireOp",EDGE,"E0");Q7=makeQuery(id+"F0.imprint","IMPRINT",FACE,{"disambiguationData":[TD([[makeQuery(id+"F0.imprint","IMPRINT",EDGE,{"derivedFrom":subQ4}),1.0]])]});}
            var Q8;
            Q8=makeQuery(id+"F0.imprint","IMPRINT",FACE,{"disambiguationData":[TD([[makeQuery(id+"F0.imprint","IMPRINT",EDGE,{"derivedFrom":sQuery(id+"F0.wireOp",EDGE,"E55.MirrorCS")}),-1.0]])]});
            var Q9;
            Q9=makeQuery(id+"F0.imprint","IMPRINT",FACE,{"disambiguationData":[TD([[makeQuery(id+"F0.imprint","IMPRINT",EDGE,{"derivedFrom":sQuery(id+"F0.wireOp",EDGE,"E58.MirrorCS")}),1.0]])]});
            var Q10;
            Q10=makeQuery(id+"F0.imprint","IMPRINT",FACE,{"disambiguationData":[TD([[makeQuery(id+"F0.imprint","IMPRINT",EDGE,{"derivedFrom":sQuery(id+"F0.wireOp",EDGE,"E57.MirrorCS")}),-1.0]])]});
            var Q11;
            Q11=makeQuery(id+"F0.imprint","IMPRINT",FACE,{"disambiguationData":[TD([[makeQuery(id+"F0.imprint","IMPRINT",EDGE,{"derivedFrom":sQuery(id+"F0.wireOp",EDGE,"E59.MirrorCS")}),1.0]])]});
            var Q12;
            Q12=makeQuery(id+"F0.imprint","IMPRINT",FACE,{"disambiguationData":[TD([[makeQuery(id+"F0.imprint","IMPRINT",EDGE,{"derivedFrom":sQuery(id+"F0.wireOp",EDGE,"E122.MirrorCS")}),-1.0]])]});
            var Q13;
            Q13=makeQuery(id+"F0.imprint","IMPRINT",FACE,{"disambiguationData":[TD([[makeQuery(id+"F0.imprint","IMPRINT",EDGE,{"derivedFrom":sQuery(id+"F0.wireOp",EDGE,"E110.MirrorCS")}),1.0]])]});
            var Q14;
            Q14=makeQuery(id+"F0.imprint","IMPRINT",FACE,{"disambiguationData":[TD([[makeQuery(id+"F0.imprint","IMPRINT",EDGE,{"derivedFrom":sQuery(id+"F0.wireOp",EDGE,"E120.MirrorCS")}),-1.0]])]});
            var Q15;
            Q15=makeQuery(id+"F0.imprint","IMPRINT",FACE,{"disambiguationData":[TD([[makeQuery(id+"F0.imprint","IMPRINT",EDGE,{"derivedFrom":sQuery(id+"F0.wireOp",EDGE,"E111.MirrorCS")}),1.0]])]});
            extrude(context, id + "F1", {"entities" : qUnion([Q0, Q1, Q2, Q3, Q4, Q5, Q6, Q7, Q8, Q9, Q10, Q11, Q12, Q13, Q14, Q15]), "depth" : 25.4 * mm});
        }
        {
            var Q0;
            Q0=makeQuery(id+"F0.imprint","IMPRINT",FACE,{"disambiguationData":[TD([[makeQuery(id+"F0.imprint","IMPRINT",EDGE,{"derivedFrom":sQuery(id+"F0.wireOp",EDGE,"E42.MirrorCS")}),-1.0]])]});
            var Q1;
            Q1=makeQuery(id+"F0.imprint","IMPRINT",FACE,{"disambiguationData":[TD([[makeQuery(id+"F0.imprint","IMPRINT",EDGE,{"derivedFrom":sQuery(id+"F0.wireOp",EDGE,"E30.MirrorCS")}),1.0]])]});
            var Q2;
            Q2=makeQuery(id+"F0.imprint","IMPRINT",FACE,{"disambiguationData":[TD([[makeQuery(id+"F0.imprint","IMPRINT",EDGE,{"derivedFrom":sQuery(id+"F0.wireOp",EDGE,"E15.MirrorCS")}),-1.0]])]});
            var Q3;
            Q3=makeQuery(id+"F0.imprint","IMPRINT",FACE,{"disambiguationData":[TD([[makeQuery(id+"F0.imprint","IMPRINT",EDGE,{"derivedFrom":sQuery(id+"F0.wireOp",EDGE,"E3")}),1.0]])]});
            var Q4;
            Q4=makeQuery(id+"F0.imprint","IMPRINT",FACE,{"disambiguationData":[TD([[makeQuery(id+"F0.imprint","IMPRINT",EDGE,{"derivedFrom":sQuery(id+"F0.wireOp",EDGE,"E76.MirrorCS")}),-1.0]])]});
            var Q5;
            {var subQ0=sQuery(id+"F0.wireOp",EDGE,"E68.MirrorCS");Q5=makeQuery(id+"F0.imprint","IMPRINT",FACE,{"disambiguationData":[TD([[makeQuery(id+"F0.imprint","IMPRINT",EDGE,{"derivedFrom":subQ0}),-1.0]])]});}
            var Q6;
            Q6=makeQuery(id+"F0.imprint","IMPRINT",FACE,{"disambiguationData":[TD([[makeQuery(id+"F0.imprint","IMPRINT",EDGE,{"derivedFrom":sQuery(id+"F0.wireOp",EDGE,"E70.MirrorCS")}),-1.0]])]});
            var Q7;
            {var subQ0=sQuery(id+"F0.wireOp",EDGE,"E60.MirrorCS");Q7=makeQuery(id+"F0.imprint","IMPRINT",FACE,{"disambiguationData":[TD([[makeQuery(id+"F0.imprint","IMPRINT",EDGE,{"derivedFrom":subQ0}),-1.0]])]});}
            var Q8;
            {var subQ0=sQuery(id+"F0.wireOp",EDGE,"E135.MirrorCS");Q8=makeQuery(id+"F0.imprint","IMPRINT",FACE,{"disambiguationData":[TD([[makeQuery(id+"F0.imprint","IMPRINT",EDGE,{"derivedFrom":subQ0}),1.0]])]});}
            var Q9;
            Q9=makeQuery(id+"F0.imprint","IMPRINT",FACE,{"disambiguationData":[TD([[makeQuery(id+"F0.imprint","IMPRINT",EDGE,{"derivedFrom":sQuery(id+"F0.wireOp",EDGE,"E136.MirrorCS")}),1.0]])]});
            var Q10;
            Q10=makeQuery(id+"F0.imprint","IMPRINT",FACE,{"disambiguationData":[TD([[makeQuery(id+"F0.imprint","IMPRINT",EDGE,{"derivedFrom":sQuery(id+"F0.wireOp",EDGE,"E115.MirrorCS")}),-1.0]])]});
            var Q11;
            {var subQ0=sQuery(id+"F0.wireOp",EDGE,"E119.MirrorCS");Q11=makeQuery(id+"F0.imprint","IMPRINT",FACE,{"disambiguationData":[TD([[makeQuery(id+"F0.imprint","IMPRINT",EDGE,{"derivedFrom":subQ0}),-1.0]])]});}
            var Q12;
            Q12=makeQuery(id+"F0.imprint","IMPRINT",FACE,{"disambiguationData":[TD([[makeQuery(id+"F0.imprint","IMPRINT",EDGE,{"derivedFrom":sQuery(id+"F0.wireOp",EDGE,"E167.MirrorCS")}),1.0]])]});
            var Q13;
            {var subQ0=sQuery(id+"F0.wireOp",EDGE,"E169.MirrorCS");Q13=makeQuery(id+"F0.imprint","IMPRINT",FACE,{"disambiguationData":[TD([[makeQuery(id+"F0.imprint","IMPRINT",EDGE,{"derivedFrom":subQ0}),1.0]])]});}
            var Q14;
            {var subQ0=sQuery(id+"F0.wireOp",EDGE,"E165.MirrorCS");Q14=makeQuery(id+"F0.imprint","IMPRINT",FACE,{"disambiguationData":[TD([[makeQuery(id+"F0.imprint","IMPRINT",EDGE,{"derivedFrom":subQ0}),-1.0]])]});}
            var Q15;
            {var subQ0=sQuery(id+"F0.wireOp",EDGE,"E179.MirrorCS");Q15=makeQuery(id+"F0.imprint","IMPRINT",FACE,{"disambiguationData":[TD([[makeQuery(id+"F0.imprint","IMPRINT",EDGE,{"derivedFrom":subQ0}),1.0]])]});}
            extrude(context, id + "F2", {"entities" : qUnion([Q0, Q1, Q2, Q3, Q4, Q5, Q6, Q7, Q8, Q9, Q10, Q11, Q12, Q13, Q14, Q15]), "depth" : 25.4 * mm});
        }
        {
            var Q0;
            Q0 = qSketchRegion(id + "F0", true);
            extrude(context, id + "F3", {"entities" : qUnion([Q0]), "depth" : 25.4 * mm});
        }
        {
            var Q0;
            {var subQ4=sQuery(id+"F0.wireOp",EDGE,"NsR8R7MI-OF9R-Is0Y-zNu6-FUBDjrlm32RV");Q0=makeQuery(id+"F0.imprint","IMPRINT",FACE,{"disambiguationData":[TD([[makeQuery(id+"F0.imprint","IMPRINT",EDGE,{"derivedFrom":subQ4}),1.0]])]});}
            var Q1;
            {var subQ0=sQuery(id+"F0.wireOp",EDGE,"E239");Q1=makeQuery(id+"F0.imprint","IMPRINT",FACE,{"disambiguationData":[TD([[makeQuery(id+"F0.imprint","IMPRINT",EDGE,{"derivedFrom":subQ0}),-1.0]])]});}
            extrude(context, id + "F4", {"entities" : qUnion([Q0, Q1]), "operationType" : NewBodyOperationType.ADD, "depth" : 25.4 * mm});
        }
        {
            var Q0;
            Q0=qCreatedBy(makeId("Front.planeOp"),FACE);
            var sketch = newSketch(context, id + "F5", { "sketchPlane" : qUnion([Q0])});
            skPoint(sketch, "E272.orphan", {"position": v(1280.25, -890.17) * mm});
            skArc(sketch, "E273", {"start": v(1516.36, -766.73) * mm, "mid": v(1486.6, -694.89) * mm, "end": v(1414.76, -665.13) * mm});
            skLineSegment(sketch, "E274", {"start": v(1414.76, -715.93) * mm, "end": v(1414.76, -665.13) * mm});
            skLineSegment(sketch, "E275.trimOffspring", {"start": v(1465.56, -766.73) * mm, "end": v(1516.36, -766.73) * mm});
            skArc(sketch, "E276.trimOffspring", {"start": v(1465.56, -766.73) * mm, "mid": v(1450.68, -730.8) * mm, "end": v(1414.76, -715.93) * mm});
            skPoint(sketch, "E277.start.orphan", {"position": v(1313.16, -766.73) * mm});
            skArc(sketch, "E278", {"start": v(1680.4, -228.78) * mm, "mid": v(1646.93, -147.96) * mm, "end": v(1566.1, -114.48) * mm});
            skArc(sketch, "E279", {"start": v(1794.7, -228.78) * mm, "mid": v(1727.75, -67.14) * mm, "end": v(1566.1, -0.18) * mm});
            skPoint(sketch, "E280.orphan", {"position": v(1337.5, -228.78) * mm});
            skLineSegment(sketch, "E281", {"start": v(1566.1, -0.18) * mm, "end": v(1566.1, -114.48) * mm});
            skLineSegment(sketch, "E282", {"start": v(1680.4, -228.78) * mm, "end": v(1794.7, -228.78) * mm});
            skArc(sketch, "E283", {"start": v(1724.86, -254.97) * mm, "mid": v(1737.56, -267.67) * mm, "end": v(1750.26, -254.97) * mm});
            skArc(sketch, "E284", {"start": v(1750.26, -228.78) * mm, "mid": v(1746.63, -241.88) * mm, "end": v(1750.26, -254.97) * mm});
            skArc(sketch, "E285", {"start": v(1724.86, -254.97) * mm, "mid": v(1728.5, -241.88) * mm, "end": v(1724.86, -228.78) * mm});
            skPoint(sketch, "E286.orphan", {"position": v(1737.56, -228.78) * mm});
            skPoint(sketch, "E287.start.orphan", {"position": v(1566.1, -57.33) * mm});
            skLineSegment(sketch, "E288", {"start": v(2010.68, 160.32) * mm, "end": v(2010.68, -233.1) * mm});
            skLineSegment(sketch, "E289.MirrorCS", {"start": v(2271.1, -228.78) * mm, "end": v(2271.1, -228.78) * mm});
            skLineSegment(sketch, "E290.MirrorCS", {"start": v(2455.25, -0.18) * mm, "end": v(2455.25, -44.63) * mm});
            skLineSegment(sketch, "E291.MirrorCS", {"start": v(2340.95, -228.78) * mm, "end": v(2296.5, -228.78) * mm});
            skArc(sketch, "E292.MirrorCS", {"start": v(2226.65, -228.78) * mm, "mid": v(2293.6, -67.14) * mm, "end": v(2455.25, -0.18) * mm});
            skPoint(sketch, "E293.MirrorP", {"position": v(2283.8, -228.78) * mm});
            skPoint(sketch, "E294.MirrorP", {"position": v(2455.25, -57.33) * mm});
            skArc(sketch, "E295.MirrorCS", {"start": v(2340.95, -228.78) * mm, "mid": v(2374.43, -147.96) * mm, "end": v(2455.25, -114.48) * mm});
            skArc(sketch, "E296", {"start": v(2296.5, -203.38) * mm, "mid": v(2283.8, -190.68) * mm, "end": v(2271.1, -203.38) * mm});
            skArc(sketch, "E297", {"start": v(2271.1, -228.78) * mm, "mid": v(2274.5, -216.08) * mm, "end": v(2271.1, -203.38) * mm});
            skArc(sketch, "E298", {"start": v(2296.5, -203.38) * mm, "mid": v(2293.1, -216.08) * mm, "end": v(2296.5, -228.78) * mm});
            skArc(sketch, "E299", {"start": v(2429.85, -44.63) * mm, "mid": v(2417.15, -57.33) * mm, "end": v(2429.85, -70.03) * mm});
            skArc(sketch, "E300", {"start": v(2429.85, -44.63) * mm, "mid": v(2442.55, -48.04) * mm, "end": v(2455.25, -44.63) * mm});
            skArc(sketch, "E301", {"start": v(2455.25, -70.03) * mm, "mid": v(2442.55, -66.63) * mm, "end": v(2429.85, -70.03) * mm});
            skLineSegment(sketch, "E302.trimOffspring", {"start": v(2455.25, -70.03) * mm, "end": v(2455.25, -114.48) * mm});
            skPoint(sketch, "E303.MirrorCS.start.orphan", {"position": v(2498.6, -44.63) * mm});
            skPoint(sketch, "E304.MirrorCS.end.orphan", {"position": v(2498.6, -70.03) * mm});
            skLineSegment(sketch, "E305.trimOffspring", {"start": v(2271.1, -228.78) * mm, "end": v(2226.65, -228.78) * mm});
            skPoint(sketch, "E306.MirrorCS.end.orphan", {"position": v(2271.1, -254.97) * mm});
            skPoint(sketch, "E307.MirrorCS.start.orphan", {"position": v(2296.5, -254.97) * mm});
            skLineSegment(sketch, "E308", {"start": v(2687.5, 101.2) * mm, "end": v(2687.5, -239.33) * mm});
            skLineSegment(sketch, "E309.MirrorCS", {"start": v(2919.76, -0.18) * mm, "end": v(2919.76, -44.63) * mm});
            skLineSegment(sketch, "E310.MirrorCS", {"start": v(2919.76, -70.03) * mm, "end": v(2919.76, -114.48) * mm});
            skLineSegment(sketch, "E311.MirrorCS", {"start": v(3103.91, -228.78) * mm, "end": v(3148.36, -228.78) * mm});
            skLineSegment(sketch, "E312.MirrorCS", {"start": v(3034.06, -228.78) * mm, "end": v(3078.51, -228.78) * mm});
            skPoint(sketch, "E313.MirrorP", {"position": v(2919.76, -57.33) * mm});
            skArc(sketch, "E314.MirrorCS", {"start": v(3034.06, -228.78) * mm, "mid": v(3000.58, -147.96) * mm, "end": v(2919.76, -114.48) * mm});
            skLineSegment(sketch, "E315.MirrorCS", {"start": v(3103.91, -228.78) * mm, "end": v(3103.91, -228.78) * mm});
            skPoint(sketch, "E316.MirrorP", {"position": v(2876.41, -44.63) * mm});
            skPoint(sketch, "E317.MirrorP", {"position": v(3091.21, -228.78) * mm});
            skPoint(sketch, "E318.MirrorP", {"position": v(2876.41, -70.03) * mm});
            skPoint(sketch, "E319.MirrorP", {"position": v(3103.91, -254.97) * mm});
            skArc(sketch, "E320.MirrorCS", {"start": v(3148.36, -228.78) * mm, "mid": v(3081.4, -67.14) * mm, "end": v(2919.76, -0.18) * mm});
            skPoint(sketch, "E321.MirrorP", {"position": v(3078.51, -254.97) * mm});
            skLineSegment(sketch, "E322", {"start": v(3078.51, -228.78) * mm, "end": v(3103.91, -228.78) * mm});
            skLineSegment(sketch, "E323", {"start": v(3081.87, -245.58) * mm, "end": v(3081.87, -245.58) * mm});
            skLineSegment(sketch, "E324", {"start": v(3103.91, -254.97) * mm, "end": v(3103.91, -254.18) * mm});
            skLineSegment(sketch, "E325", {"start": v(3078.51, -254.97) * mm, "end": v(3078.51, -254.18) * mm});
            skLineSegment(sketch, "E326", {"start": v(3103.91, -254.97) * mm, "end": v(3103.89, -254.97) * mm});
            skArc(sketch, "E327", {"start": v(3078.51, -254.97) * mm, "mid": v(3082.15, -241.88) * mm, "end": v(3078.51, -228.78) * mm});
            skArc(sketch, "E328", {"start": v(3103.91, -228.78) * mm, "mid": v(3100.28, -241.88) * mm, "end": v(3103.91, -254.97) * mm});
            skLineSegment(sketch, "E329.trimOffspring", {"start": v(3078.54, -254.97) * mm, "end": v(3078.51, -254.97) * mm});
            skArc(sketch, "E330.trimOffspring", {"start": v(3078.51, -254.18) * mm, "mid": v(3091.21, -266.88) * mm, "end": v(3103.91, -254.18) * mm});
            skLineSegment(sketch, "E331", {"start": v(2919.76, -44.63) * mm, "end": v(2919.76, -70.03) * mm});
            skLineSegment(sketch, "E332", {"start": v(2919.76, -57.33) * mm, "end": v(2894.36, -57.33) * mm});
            skCircle(sketch, "E333", {"center": v(2894.36, -57.33) * mm, "radius": 12.7 * mm});
            skLineSegment(sketch, "E334", {"start": v(2876.41, -70.03) * mm, "end": v(2919.76, -70.03) * mm});
            skLineSegment(sketch, "E335", {"start": v(2876.41, -44.63) * mm, "end": v(2919.76, -44.63) * mm});
            skLineSegment(sketch, "E336", {"start": v(2876.41, -44.63) * mm, "end": v(2894.36, -57.33) * mm});
            skLineSegment(sketch, "E337", {"start": v(2876.41, -70.03) * mm, "end": v(2894.36, -57.33) * mm});
            skArc(sketch, "E338", {"start": v(2876.41, -44.63) * mm, "mid": v(2898.09, -56.8) * mm, "end": v(2919.76, -44.63) * mm});
            skArc(sketch, "E339", {"start": v(1540.7, -44.63) * mm, "mid": v(1528, -57.33) * mm, "end": v(1540.7, -70.03) * mm});
            skArc(sketch, "E340", {"start": v(1566.1, -70.03) * mm, "mid": v(1553.4, -66.63) * mm, "end": v(1540.7, -70.03) * mm});
            skArc(sketch, "E341", {"start": v(1540.7, -44.63) * mm, "mid": v(1553.4, -48.04) * mm, "end": v(1566.1, -44.63) * mm});
            skSolve(sketch);
        }
        {
            var Q0;
            {var subQ4=sQuery(id+"F5.wireOp",EDGE,"E278");Q0=makeQuery(id+"F5.imprint","IMPRINT",FACE,{"disambiguationData":[TD([[makeQuery(id+"F5.imprint","IMPRINT",EDGE,{"derivedFrom":subQ4}),-1.0]])]});}
            var Q1;
            Q1=makeQuery(id+"F5.imprint","IMPRINT",FACE,{"disambiguationData":[TD([[makeQuery(id+"F5.imprint","IMPRINT",EDGE,{"derivedFrom":sQuery(id+"F5.wireOp",EDGE,"3pxmdgSV-8hSW-zAfp-bw9c-bzv8lNnqetjR")}),1.0]])]});
            var Q2;
            Q2=makeQuery(id+"F5.imprint","IMPRINT",FACE,{"disambiguationData":[TD([[makeQuery(id+"F5.imprint","IMPRINT",EDGE,{"derivedFrom":sQuery(id+"F5.wireOp",EDGE,"E283")}),1.0]])]});
            extrude(context, id + "F6", {"entities" : qUnion([Q0, Q1, Q2]), "depth" : 25.4 * mm});
        }
        {
            var Q0;
            Q0=makeQuery(id+"F5.imprint","IMPRINT",FACE,{"disambiguationData":[TD([[makeQuery(id+"F5.imprint","IMPRINT",EDGE,{"derivedFrom":sQuery(id+"F5.wireOp",EDGE,"E290.MirrorCS")}),-1.0]])]});
            extrude(context, id + "F7", {"entities" : qUnion([Q0]), "depth" : 25.4 * mm});
        }
        {
            var Q0;
            Q0=makeQuery(id+"F5.imprint","IMPRINT",FACE,{"disambiguationData":[TD([[makeQuery(id+"F5.imprint","IMPRINT",EDGE,{"derivedFrom":sQuery(id+"F5.wireOp",EDGE,"5b398558-4a1d-42fb-8e60-ba96c2d905250.MirrorCS")}),-1.0]])]});
            var Q1;
            {var subQ5=sQuery(id+"F5.wireOp",EDGE,"E322");Q1=makeQuery(id+"F5.imprint","IMPRINT",FACE,{"disambiguationData":[TD([[makeQuery(id+"F5.imprint","IMPRINT",EDGE,{"derivedFrom":subQ5}),-1.0]])]});}
            extrude(context, id + "F8", {"entities" : qUnion([Q0, Q1]), "depth" : 25.4 * mm});
        }
        {
            var Q0;
            Q0=makeQuery(id+"F5.imprint","IMPRINT",FACE,{"disambiguationData":[TD([[makeQuery(id+"F5.imprint","IMPRINT",EDGE,{"derivedFrom":sQuery(id+"F5.wireOp",EDGE,"E339")}),1.0]])]});
            extrude(context, id + "F9", {"entities" : qUnion([Q0]), "operationType" : NewBodyOperationType.ADD, "depth" : 25.4 * mm});
        }
    });
